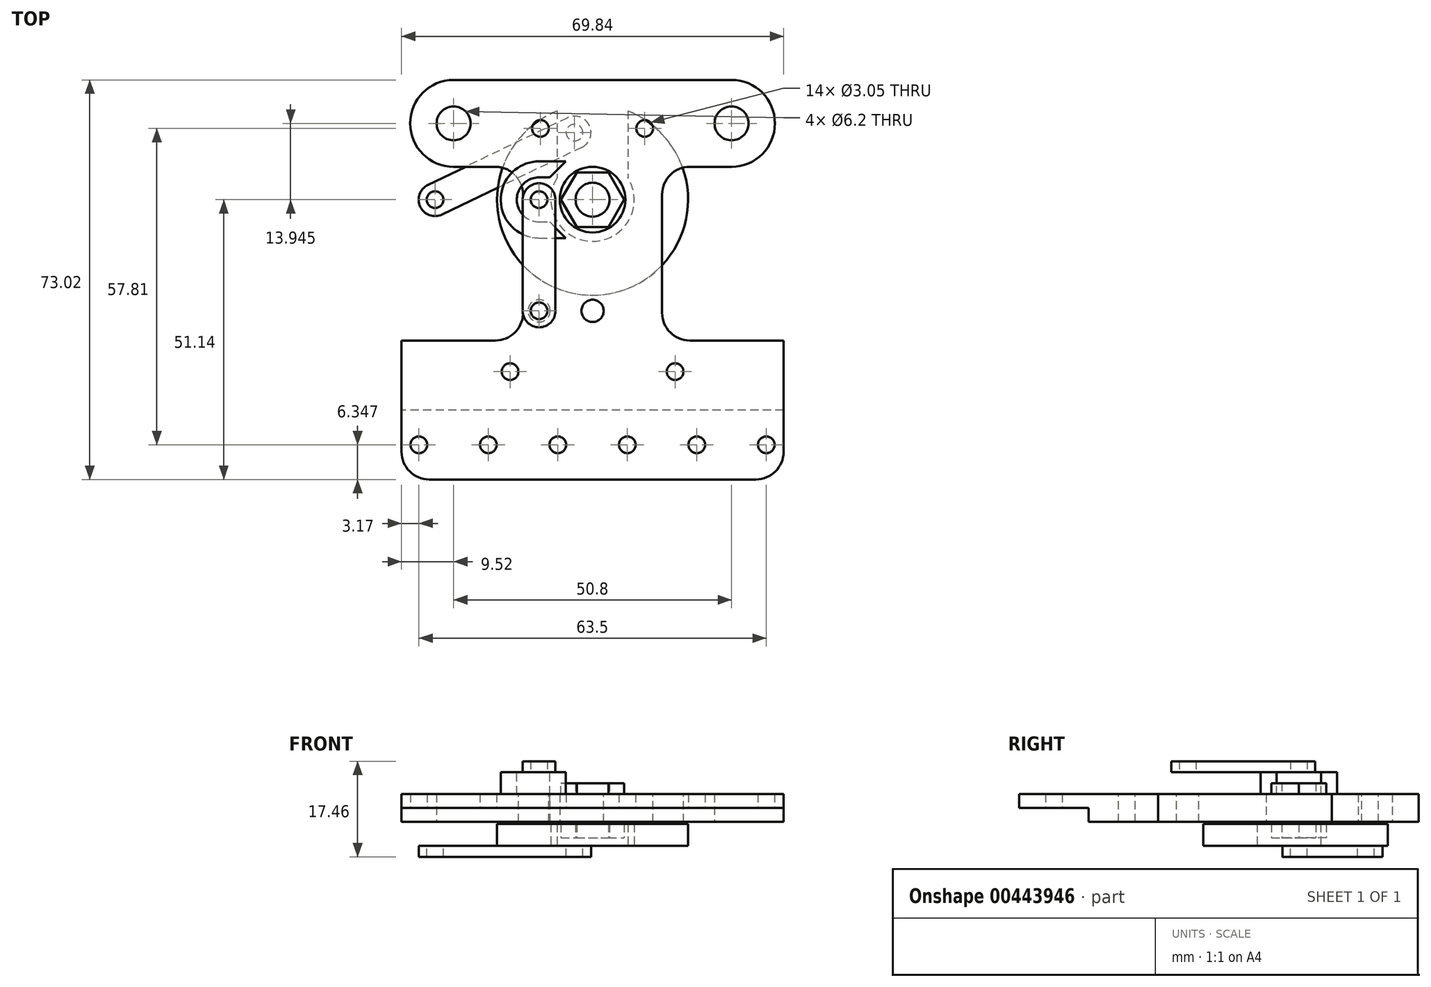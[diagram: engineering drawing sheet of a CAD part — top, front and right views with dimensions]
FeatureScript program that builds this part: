
annotation { "Feature Type Name" : "Feature", "Feature Type Description" : "" }
export const myFeature = defineFeature(function(context is Context, id is Id, definition is map)
    precondition{}
    {
        {
            var Q0;
            Q0=qCreatedBy(makeId("Top.planeOp"),FACE);
            var sketch = newSketch(context, id + "F0", { "sketchPlane" : qUnion([Q0])});
            skLineSegment(sketch, "E0.bottom", {"start": v(-34.92, 36.51) * mm, "end": v(34.93, 36.51) * mm});
            skLineSegment(sketch, "E0.top", {"start": v(-34.93, -36.51) * mm, "end": v(34.92, -36.51) * mm});
            skLineSegment(sketch, "E0.left", {"start": v(-34.92, 36.51) * mm, "end": v(-34.93, -36.51) * mm});
            skLineSegment(sketch, "E0.right", {"start": v(34.93, 36.51) * mm, "end": v(34.92, -36.51) * mm});
            skPoint(sketch, "E0.middle", {"position": v(0, 0) * mm});
            skSolve(sketch);
        }
        {
            var Q0;
            Q0=qSketchRegion(id+"F0",true);
            extrude(context, id + "F1", {"entities" : qUnion([Q0]), "depth" : 5.08 * mm});
        }
        {
            var Q0;
            Q0=makeQuery(id+"F1.opExtrude","SWEPT_FACE",FACE,{"disambiguationData":[OSD([sQuery(id+"F0.wireOp",EDGE,"E0.left")])]});
            var sketch = newSketch(context, id + "F2", { "sketchPlane" : qUnion([Q0])});
            skLineSegment(sketch, "E1.bottom", {"start": v(36.51, 2.54) * mm, "end": v(23.81, 2.54) * mm});
            skLineSegment(sketch, "E1.top", {"start": v(36.51, 0) * mm, "end": v(23.81, 0) * mm});
            skLineSegment(sketch, "E1.left", {"start": v(36.51, 2.54) * mm, "end": v(36.51, 0) * mm});
            skLineSegment(sketch, "E1.right", {"start": v(23.81, 2.54) * mm, "end": v(23.81, 0) * mm});
            skSolve(sketch);
        }
        {
            var Q0;
            Q0=qSketchRegion(id+"F2",true);
            extrude(context, id + "F3", {"entities" : qUnion([Q0]), "operationType" : NewBodyOperationType.REMOVE, "endBound" : BoundingType.THROUGH_ALL, "oppositeDirection" : true, "depth" : 25.4 * mm});
        }
        {
            var Q0;
            Q0=makeQuery(id+"F1.opExtrude","CAP_FACE",FACE,{"disambiguationData":[OSD([sQuery(id+"F0.wireOp",EDGE,"E0.bottom"),sQuery(id+"F0.wireOp",EDGE,"E0.top"),sQuery(id+"F0.wireOp",EDGE,"E0.left"),sQuery(id+"F0.wireOp",EDGE,"E0.right")])],"isStart":true});
            var sketch = newSketch(context, id + "F4", { "sketchPlane" : qUnion([Q0])});
            skLineSegment(sketch, "E2", {"start": v(-25.4, -28.58) * mm, "end": v(0, -28.58) * mm, "construction": true});
            skLineSegment(sketch, "E3", {"start": v(0, -28.58) * mm, "end": v(25.4, -28.58) * mm, "construction": true});
            skLineSegment(sketch, "E4", {"start": v(0, -28.58) * mm, "end": v(0, -14.63) * mm, "construction": true});
            skCircle(sketch, "E5", {"center": v(-25.4, -28.58) * mm, "radius": 3.1 * mm});
            skCircle(sketch, "E6", {"center": v(0, -14.63) * mm, "radius": 6 * mm});
            skCircle(sketch, "E7", {"center": v(25.4, -28.58) * mm, "radius": 3.1 * mm});
            skArc(sketch, "E8", {"start": v(-25.4, -36.51) * mm, "mid": v(-33.34, -28.58) * mm, "end": v(-25.4, -20.64) * mm});
            skArc(sketch, "E9", {"start": v(25.4, -36.51) * mm, "mid": v(33.34, -28.58) * mm, "end": v(25.4, -20.64) * mm});
            skLineSegment(sketch, "E10", {"start": v(-25.4, -20.64) * mm, "end": v(-12.7, -20.64) * mm});
            skLineSegment(sketch, "E11", {"start": v(-12.7, -20.64) * mm, "end": v(-12.7, 11.11) * mm});
            skLineSegment(sketch, "E12", {"start": v(-12.7, 11.11) * mm, "end": v(-34.93, 11.11) * mm});
            skLineSegment(sketch, "E13", {"start": v(12.7, 11.11) * mm, "end": v(34.92, 11.11) * mm});
            skLineSegment(sketch, "E14", {"start": v(34.92, 11.11) * mm, "end": v(34.93, -36.51) * mm});
            skLineSegment(sketch, "E15", {"start": v(34.93, -36.51) * mm, "end": v(25.4, -36.51) * mm});
            skLineSegment(sketch, "E16", {"start": v(-25.4, -36.51) * mm, "end": v(-34.92, -36.51) * mm});
            skLineSegment(sketch, "E17", {"start": v(-34.92, -36.51) * mm, "end": v(-34.93, 11.11) * mm});
            skLineSegment(sketch, "E18", {"start": v(25.4, -20.64) * mm, "end": v(12.7, -20.64) * mm});
            skLineSegment(sketch, "E19", {"start": v(12.7, -20.64) * mm, "end": v(12.7, 11.11) * mm});
            skLineSegment(sketch, "E20", {"start": v(-25.4, -28.58) * mm, "end": v(-25.4, -14.63) * mm, "construction": true});
            skLineSegment(sketch, "E21", {"start": v(0, -14.63) * mm, "end": v(-12.7, -14.63) * mm, "construction": true});
            skLineSegment(sketch, "E22", {"start": v(0, -14.63) * mm, "end": v(12.7, -14.63) * mm, "construction": true});
            skSolve(sketch);
        }
        {
            var Q0;
            Q0=qSketchRegion(id+"F4",true);
            extrude(context, id + "F5", {"entities" : qUnion([Q0]), "operationType" : NewBodyOperationType.REMOVE, "endBound" : BoundingType.UP_TO_NEXT, "oppositeDirection" : true, "depth" : 25.4 * mm});
        }
        {
            var Q0;
            Q0=makeQuery(id+"F5.boolean.opBoolean","COPY",EDGE,{"derivedFrom":makeQuery(id+"F5.opExtrude","SWEPT_EDGE",EDGE,{"disambiguationData":[OSD([sQuery(id+"F4.wireOp",EDGE,"E10"),sQuery(id+"F4.wireOp",EDGE,"E11")])]})});
            var Q1;
            Q1=makeQuery(id+"F5.boolean.opBoolean","COPY",EDGE,{"derivedFrom":makeQuery(id+"F5.opExtrude","SWEPT_EDGE",EDGE,{"disambiguationData":[OSD([sQuery(id+"F4.wireOp",EDGE,"E18"),sQuery(id+"F4.wireOp",EDGE,"E19")])]})});
            var Q2;
            Q2=makeQuery(id+"F5.boolean.opBoolean","COPY",EDGE,{"derivedFrom":makeQuery(id+"F5.opExtrude","SWEPT_EDGE",EDGE,{"disambiguationData":[OSD([sQuery(id+"F4.wireOp",EDGE,"E13"),sQuery(id+"F4.wireOp",EDGE,"E19")])]})});
            var Q3;
            Q3=makeQuery(id+"F5.boolean.opBoolean","COPY",EDGE,{"derivedFrom":makeQuery(id+"F5.opExtrude","SWEPT_EDGE",EDGE,{"disambiguationData":[OSD([sQuery(id+"F4.wireOp",EDGE,"E11"),sQuery(id+"F4.wireOp",EDGE,"E12")])]})});
            var Q4;
            Q4=makeQuery(id+"F5.boolean.opBoolean","COPY",EDGE,{"derivedFrom":makeQuery(id+"F5.opExtrude","SWEPT_EDGE",EDGE,{"disambiguationData":[OSD([sQuery(id+"F0.wireOp",EDGE,"E0.right"),sQuery(id+"F4.wireOp",EDGE,"E13"),sQuery(id+"F4.wireOp",EDGE,"E14")])]})});
            var Q5;
            Q5=makeQuery(id+"F5.boolean.opBoolean","COPY",EDGE,{"derivedFrom":makeQuery(id+"F5.opExtrude","SWEPT_EDGE",EDGE,{"disambiguationData":[OSD([sQuery(id+"F0.wireOp",EDGE,"E0.left"),sQuery(id+"F4.wireOp",EDGE,"E12"),sQuery(id+"F4.wireOp",EDGE,"E17")])]})});
            var Q6;
            Q6=makeQuery(id+"F1.opExtrude","SWEPT_EDGE",EDGE,{"disambiguationData":[OSD([sQuery(id+"F0.wireOp",EDGE,"E0.top"),sQuery(id+"F0.wireOp",EDGE,"E0.left")])]});
            var Q7;
            Q7=makeQuery(id+"F1.opExtrude","SWEPT_EDGE",EDGE,{"disambiguationData":[OSD([sQuery(id+"F0.wireOp",EDGE,"E0.top"),sQuery(id+"F0.wireOp",EDGE,"E0.right")])]});
            fillet(context, id + "F6", {"entities" : qUnion([Q0, Q1, Q2, Q3, Q4, Q5, Q6, Q7]), "radius" : 5.08 * mm, "tangentPropagation" : true, "allowEdgeOverflow" : false});
        }
        {
            var Q0;
            Q0=makeQuery(id+"F1.opExtrude","CAP_FACE",FACE,{"disambiguationData":[OSD([sQuery(id+"F0.wireOp",EDGE,"E0.bottom"),sQuery(id+"F0.wireOp",EDGE,"E0.top"),sQuery(id+"F0.wireOp",EDGE,"E0.left"),sQuery(id+"F0.wireOp",EDGE,"E0.right")])],"isStart":true});
            cPlane(context, id + "F7", {"entities" : qUnion([Q0]), "cplaneType" : CPlaneType.OFFSET, "offset" : 0.38 * mm, "width" : 152.4 * mm, "height" : 152.4 * mm});
        }
        {
            var Q0;
            Q0=qCreatedBy(id+"F7.planeOp",FACE);
            var sketch = newSketch(context, id + "F8", { "sketchPlane" : qUnion([Q0])});
            skCircle(sketch, "E23", {"center": v(0, -14.63) * mm, "radius": 17.46 * mm});
            skSolve(sketch);
        }
        {
            var Q0;
            Q0=makeQuery(id+"F8.imprint","IMPRINT",FACE,{"disambiguationData":[TD([[makeQuery(id+"F8.imprint","IMPRINT",EDGE,{"derivedFrom":sQuery(id+"F8.wireOp",EDGE,"7JbUnUjg-stlZ-eKcx-IOZO-H9E1dYresgRF.bottom")}),-1.0]])]});
            var Q1;
            Q1=makeQuery(id+"F8.imprint","IMPRINT",FACE,{"disambiguationData":[TD([[makeQuery(id+"F8.imprint","IMPRINT",EDGE,{"derivedFrom":sQuery(id+"F8.wireOp",EDGE,"E23")}),1.0]])]});
            var Q2;
            Q2=sQuery(id+"F8.wireOp",EDGE,"7JbUnUjg-stlZ-eKcx-IOZO-H9E1dYresgRF.bottom");
            var Q3;
            Q3=sQuery(id+"F8.wireOp",EDGE,"7JbUnUjg-stlZ-eKcx-IOZO-H9E1dYresgRF.top");
            extrude(context, id + "F9", {"entities" : qUnion([Q0, Q1]), "surfaceEntities" : qUnion([Q2, Q3]), "depth" : 4 * mm});
        }
        {
            var Q0;
            Q0=makeQuery(id+"F9.opExtrude","CAP_FACE",FACE,{"disambiguationData":[OSD([sQuery(id+"F8.wireOp",EDGE,"E23")])],"isStart":false});
            var sketch = newSketch(context, id + "F10", { "sketchPlane" : qUnion([Q0])});
            skCircle(sketch, "E24", {"center": v(0, -14.63) * mm, "radius": 3.1 * mm});
            skSolve(sketch);
        }
        {
            var Q0;
            Q0=makeQuery(id+"F10.imprint","IMPRINT",FACE,{"disambiguationData":[TD([[makeQuery(id+"F10.imprint","IMPRINT",EDGE,{"derivedFrom":sQuery(id+"F10.wireOp",EDGE,"E24")}),1.0]])]});
            extrude(context, id + "F11", {"entities" : qUnion([Q0]), "operationType" : NewBodyOperationType.REMOVE, "oppositeDirection" : true, "depth" : 25.4 * mm});
        }
        {
            var Q0;
            Q0=makeQuery(id+"F9.opExtrude","CAP_FACE",FACE,{"disambiguationData":[OSD([sQuery(id+"F8.wireOp",EDGE,"E23")])],"isStart":false});
            var sketch = newSketch(context, id + "F12", { "sketchPlane" : qUnion([Q0])});
            skCircle(sketch, "E25.cCircle", {"center": v(0, -14.63) * mm, "radius": 5 * mm, "construction": true});
            skLineSegment(sketch, "E25.0", {"start": v(2.89, -9.63) * mm, "end": v(5.77, -14.63) * mm});
            skLineSegment(sketch, "E25.1", {"start": v(5.77, -14.63) * mm, "end": v(2.89, -19.63) * mm});
            skLineSegment(sketch, "E25.2", {"start": v(2.89, -19.63) * mm, "end": v(-2.89, -19.63) * mm});
            skLineSegment(sketch, "E25.3", {"start": v(-2.89, -19.63) * mm, "end": v(-5.77, -14.63) * mm});
            skLineSegment(sketch, "E25.4", {"start": v(-5.77, -14.63) * mm, "end": v(-2.89, -9.63) * mm});
            skLineSegment(sketch, "E25.5", {"start": v(-2.89, -9.63) * mm, "end": v(2.89, -9.63) * mm});
            skPoint(sketch, "E25.0.midPoint", {"position": v(4.33, -12.13) * mm});
            skSolve(sketch);
        }
        {
            var Q0;
            Q0=makeQuery(id+"F3.boolean.opBoolean","COPY",FACE,{"derivedFrom":makeQuery(id+"F3.opExtrude","SWEPT_FACE",FACE,{"disambiguationData":[OSD([sQuery(id+"F2.wireOp",EDGE,"E1.bottom")])]})});
            var sketch = newSketch(context, id + "F13", { "sketchPlane" : qUnion([Q0])});
            skLineSegment(sketch, "E26", {"start": v(-31.75, 30.16) * mm, "end": v(-19.05, 30.16) * mm, "construction": true});
            skLineSegment(sketch, "E27", {"start": v(-19.05, 30.16) * mm, "end": v(-6.35, 30.16) * mm, "construction": true});
            skLineSegment(sketch, "E28", {"start": v(-6.35, 30.16) * mm, "end": v(6.35, 30.16) * mm, "construction": true});
            skLineSegment(sketch, "E29", {"start": v(6.35, 30.16) * mm, "end": v(19.05, 30.16) * mm, "construction": true});
            skLineSegment(sketch, "E30", {"start": v(19.05, 30.16) * mm, "end": v(31.75, 30.16) * mm, "construction": true});
            skLineSegment(sketch, "E31", {"start": v(31.75, 30.16) * mm, "end": v(34.92, 30.16) * mm, "construction": true});
            skLineSegment(sketch, "E32", {"start": v(-31.75, 30.16) * mm, "end": v(-34.93, 30.16) * mm, "construction": true});
            skCircle(sketch, "E33", {"center": v(-31.75, 30.16) * mm, "radius": 1.52 * mm});
            skCircle(sketch, "E34", {"center": v(-19.05, 30.16) * mm, "radius": 1.52 * mm});
            skCircle(sketch, "E35", {"center": v(-6.35, 30.16) * mm, "radius": 1.52 * mm});
            skCircle(sketch, "E36", {"center": v(6.35, 30.16) * mm, "radius": 1.52 * mm});
            skCircle(sketch, "E37", {"center": v(19.05, 30.16) * mm, "radius": 1.52 * mm});
            skCircle(sketch, "E38", {"center": v(31.75, 30.16) * mm, "radius": 1.52 * mm});
            skLineSegment(sketch, "E39", {"start": v(-29.85, 36.51) * mm, "end": v(-29.85, 23.81) * mm, "construction": true});
            skPoint(sketch, "E40", {"position": v(-29.85, 30.16) * mm});
            skSolve(sketch);
        }
        {
            var Q0;
            Q0=makeQuery(id+"F12.imprint","IMPRINT",FACE,{"disambiguationData":[TD([[makeQuery(id+"F12.imprint","IMPRINT",EDGE,{"derivedFrom":sQuery(id+"F12.wireOp",EDGE,"E25.0")}),-1.0]])]});
            extrude(context, id + "F14", {"entities" : qUnion([Q0]), "operationType" : NewBodyOperationType.REMOVE, "oppositeDirection" : true, "depth" : 1.5 * mm});
        }
        {
            var Q0;
            Q0=makeQuery(id+"F9.opExtrude","CAP_FACE",FACE,{"disambiguationData":[OSD([sQuery(id+"F8.wireOp",EDGE,"E23")])],"isStart":false});
            var sketch = newSketch(context, id + "F15", { "sketchPlane" : qUnion([Q0])});
            skLineSegment(sketch, "E41", {"start": v(0, -14.63) * mm, "end": v(-3.29, -26.9) * mm, "construction": true});
            skLineSegment(sketch, "E42", {"start": v(-25.4, -28.58) * mm, "end": v(-25.4, -14.63) * mm, "construction": true});
            skLineSegment(sketch, "E43", {"start": v(-25.4, -14.63) * mm, "end": v(-28.78, -14.63) * mm, "construction": true});
            skLineSegment(sketch, "E44", {"start": v(-28.78, -14.63) * mm, "end": v(-3.29, -26.9) * mm, "construction": true});
            skLineSegment(sketch, "E45", {"start": v(0, -14.63) * mm, "end": v(3.29, -26.9) * mm, "construction": true});
            skCircle(sketch, "E46", {"center": v(-3.29, -26.9) * mm, "radius": 1.52 * mm});
            skCircle(sketch, "E47", {"center": v(3.29, -26.9) * mm, "radius": 1.52 * mm});
            skSolve(sketch);
        }
        {
            var Q0;
            Q0=makeQuery(id+"F15.imprint","IMPRINT",FACE,{"disambiguationData":[TD([[makeQuery(id+"F15.imprint","IMPRINT",EDGE,{"derivedFrom":sQuery(id+"F15.wireOp",EDGE,"E46")}),1.0]])]});
            var Q1;
            Q1=makeQuery(id+"F15.imprint","IMPRINT",FACE,{"disambiguationData":[TD([[makeQuery(id+"F15.imprint","IMPRINT",EDGE,{"derivedFrom":sQuery(id+"F15.wireOp",EDGE,"E47")}),1.0]])]});
            var Q2;
            Q2=sQuery(id+"F15.wireOp",EDGE,"E44");
            var Q3;
            Q3=sQuery(id+"F15.wireOp",EDGE,"E41");
            var Q4;
            Q4=sQuery(id+"F15.wireOp",EDGE,"E45");
            var Q5;
            Q5=sQuery(id+"F15.wireOp",EDGE,"E43");
            var Q6;
            Q6=sQuery(id+"F15.wireOp",EDGE,"E42");
            extrude(context, id + "F16", {"entities" : qUnion([Q0, Q1]), "operationType" : NewBodyOperationType.REMOVE, "surfaceEntities" : qUnion([Q2, Q3, Q4, Q5, Q6]), "endBound" : BoundingType.UP_TO_NEXT, "oppositeDirection" : true, "depth" : 25.4 * mm});
        }
        {
            var Q0;
            Q0=makeQuery(id+"F9.opExtrude","CAP_FACE",FACE,{"disambiguationData":[OSD([sQuery(id+"F8.wireOp",EDGE,"E23")])],"isStart":false});
            var sketch = newSketch(context, id + "F17", { "sketchPlane" : qUnion([Q0])});
            skArc(sketch, "E48", {"start": v(-6.48, -18.64) * mm, "mid": v(0, -7.01) * mm, "end": v(6.48, -18.64) * mm});
            skLineSegment(sketch, "E49", {"start": v(-6.48, -18.64) * mm, "end": v(-6.48, -30.85) * mm});
            skLineSegment(sketch, "E50", {"start": v(6.48, -18.64) * mm, "end": v(6.48, -30.85) * mm});
            skSolve(sketch);
        }
        {
            var Q0;
            Q0=qSketchRegion(id+"F17",true);
            var Q1;
            Q1=makeQuery(id+"F17.imprint","IMPRINT",FACE,{"disambiguationData":[TD([[makeQuery(id+"F17.imprint","IMPRINT",EDGE,{"derivedFrom":sQuery(id+"F17.wireOp",EDGE,"E48")}),1.0]])]});
            extrude(context, id + "F18", {"entities" : qUnion([Q0, Q1]), "operationType" : NewBodyOperationType.REMOVE, "endBound" : BoundingType.UP_TO_NEXT, "oppositeDirection" : true, "depth" : 25.4 * mm});
        }
        {
            var Q0;
            Q0=makeQuery(id+"F9.opExtrude","CAP_FACE",FACE,{"disambiguationData":[OSD([sQuery(id+"F8.wireOp",EDGE,"E23")])],"isStart":false});
            var sketch = newSketch(context, id + "F19", { "sketchPlane" : qUnion([Q0])});
            skLineSegment(sketch, "E51", {"start": v(-3.29, -26.9) * mm, "end": v(-28.78, -14.63) * mm, "construction": true});
            skLineSegment(sketch, "E52", {"start": v(-28.78, -14.63) * mm, "end": v(-25.4, -14.63) * mm, "construction": true});
            skLineSegment(sketch, "E53", {"start": v(-25.4, -14.63) * mm, "end": v(-25.4, -28.58) * mm, "construction": true});
            skArc(sketch, "E54", {"start": v(-30.08, -17.33) * mm, "mid": v(-31.48, -13.33) * mm, "end": v(-27.48, -11.93) * mm});
            skArc(sketch, "E55", {"start": v(-1.99, -24.2) * mm, "mid": v(-0.58, -28.2) * mm, "end": v(-4.59, -29.6) * mm});
            skLineSegment(sketch, "E56", {"start": v(-1.99, -24.2) * mm, "end": v(-27.48, -11.93) * mm});
            skLineSegment(sketch, "E57", {"start": v(-4.59, -29.6) * mm, "end": v(-30.08, -17.33) * mm});
            skCircle(sketch, "E58", {"center": v(-3.29, -26.9) * mm, "radius": 1.52 * mm});
            skCircle(sketch, "E59", {"center": v(-28.78, -14.63) * mm, "radius": 1.52 * mm});
            skSolve(sketch);
        }
        {
            var Q0;
            Q0=qSketchRegion(id+"F19",true);
            extrude(context, id + "F20", {"entities" : qUnion([Q0]), "depth" : 2 * mm});
        }
        {
            var Q0;
            Q0=makeQuery(id+"F13.imprint","IMPRINT",FACE,{"disambiguationData":[TD([[makeQuery(id+"F13.imprint","IMPRINT",EDGE,{"derivedFrom":sQuery(id+"F13.wireOp",EDGE,"E33")}),1.0]])]});
            var Q1;
            Q1=makeQuery(id+"F13.imprint","IMPRINT",FACE,{"disambiguationData":[TD([[makeQuery(id+"F13.imprint","IMPRINT",EDGE,{"derivedFrom":sQuery(id+"F13.wireOp",EDGE,"E34")}),1.0]])]});
            var Q2;
            Q2=makeQuery(id+"F13.imprint","IMPRINT",FACE,{"disambiguationData":[TD([[makeQuery(id+"F13.imprint","IMPRINT",EDGE,{"derivedFrom":sQuery(id+"F13.wireOp",EDGE,"E35")}),1.0]])]});
            var Q3;
            Q3=makeQuery(id+"F13.imprint","IMPRINT",FACE,{"disambiguationData":[TD([[makeQuery(id+"F13.imprint","IMPRINT",EDGE,{"derivedFrom":sQuery(id+"F13.wireOp",EDGE,"E36")}),1.0]])]});
            var Q4;
            Q4=makeQuery(id+"F13.imprint","IMPRINT",FACE,{"disambiguationData":[TD([[makeQuery(id+"F13.imprint","IMPRINT",EDGE,{"derivedFrom":sQuery(id+"F13.wireOp",EDGE,"E37")}),1.0]])]});
            var Q5;
            Q5=makeQuery(id+"F13.imprint","IMPRINT",FACE,{"disambiguationData":[TD([[makeQuery(id+"F13.imprint","IMPRINT",EDGE,{"derivedFrom":sQuery(id+"F13.wireOp",EDGE,"E38")}),1.0]])]});
            extrude(context, id + "F21", {"entities" : qUnion([Q0, Q1, Q2, Q3, Q4, Q5]), "operationType" : NewBodyOperationType.REMOVE, "endBound" : BoundingType.UP_TO_NEXT, "oppositeDirection" : true, "depth" : 25.4 * mm});
        }
        {
            var Q0;
            Q0=makeQuery(id+"F1.opExtrude","CAP_FACE",FACE,{"disambiguationData":[OSD([sQuery(id+"F0.wireOp",EDGE,"E0.bottom"),sQuery(id+"F0.wireOp",EDGE,"E0.top"),sQuery(id+"F0.wireOp",EDGE,"E0.left"),sQuery(id+"F0.wireOp",EDGE,"E0.right")])],"isStart":false});
            var sketch = newSketch(context, id + "F22", { "sketchPlane" : qUnion([Q0])});
            skCircle(sketch, "E60", {"center": v(0, 14.63) * mm, "radius": 3.1 * mm});
            skCircle(sketch, "E61", {"center": v(-9.78, 14.63) * mm, "radius": 1.52 * mm});
            skLineSegment(sketch, "E62", {"start": v(-9.78, 14.63) * mm, "end": v(0, 14.63) * mm, "construction": true});
            skLineSegment(sketch, "E63.bottom", {"start": v(-9.78, 21.63) * mm, "end": v(0, 21.63) * mm});
            skLineSegment(sketch, "E63.top", {"start": v(-9.78, 7.63) * mm, "end": v(0, 7.63) * mm});
            skLineSegment(sketch, "E63.left", {"start": v(-9.78, 21.63) * mm, "end": v(-9.78, 7.63) * mm, "construction": true});
            skLineSegment(sketch, "E63.right", {"start": v(0, 21.63) * mm, "end": v(0, 7.63) * mm, "construction": true});
            skPoint(sketch, "E63.middle", {"position": v(-4.89, 14.63) * mm});
            skArc(sketch, "E64", {"start": v(-9.78, 7.63) * mm, "mid": v(-16.78, 14.63) * mm, "end": v(-9.78, 21.63) * mm});
            skArc(sketch, "E65", {"start": v(0, 21.63) * mm, "mid": v(7, 14.63) * mm, "end": v(0, 7.63) * mm});
            skSolve(sketch);
        }
        {
            var Q0;
            Q0=qSketchRegion(id+"F22",true);
            extrude(context, id + "F23", {"entities" : qUnion([Q0]), "depth" : 4 * mm});
        }
        {
            var Q0;
            Q0=makeQuery(id+"F23.opExtrude","CAP_FACE",FACE,{"disambiguationData":[OSD([sQuery(id+"F22.wireOp",EDGE,"E60"),sQuery(id+"F22.wireOp",EDGE,"E61"),sQuery(id+"F22.wireOp",EDGE,"E63.bottom"),sQuery(id+"F22.wireOp",EDGE,"E63.top"),sQuery(id+"F22.wireOp",EDGE,"E64"),sQuery(id+"F22.wireOp",EDGE,"E65")])],"isStart":false});
            var sketch = newSketch(context, id + "F24", { "sketchPlane" : qUnion([Q0])});
            skCircle(sketch, "E66.cCircle", {"center": v(0, 14.63) * mm, "radius": 5 * mm, "construction": true});
            skLineSegment(sketch, "E66.0", {"start": v(-2.89, 19.63) * mm, "end": v(2.89, 19.63) * mm});
            skLineSegment(sketch, "E66.1", {"start": v(2.89, 19.63) * mm, "end": v(5.77, 14.63) * mm});
            skLineSegment(sketch, "E66.2", {"start": v(5.77, 14.63) * mm, "end": v(2.89, 9.63) * mm});
            skLineSegment(sketch, "E66.3", {"start": v(2.89, 9.63) * mm, "end": v(-2.89, 9.63) * mm});
            skLineSegment(sketch, "E66.4", {"start": v(-2.89, 9.63) * mm, "end": v(-5.77, 14.63) * mm});
            skLineSegment(sketch, "E66.5", {"start": v(-5.77, 14.63) * mm, "end": v(-2.89, 19.63) * mm});
            skPoint(sketch, "E66.0.midPoint", {"position": v(0, 19.63) * mm});
            skSolve(sketch);
        }
        {
            var Q0;
            Q0=qSketchRegion(id+"F24",true);
            extrude(context, id + "F25", {"entities" : qUnion([Q0]), "operationType" : NewBodyOperationType.REMOVE, "oppositeDirection" : true, "depth" : 2 * mm});
        }
        {
            var Q0;
            Q0=makeQuery(id+"F23.opExtrude","CAP_FACE",FACE,{"disambiguationData":[OSD([sQuery(id+"F22.wireOp",EDGE,"E60"),sQuery(id+"F22.wireOp",EDGE,"E61"),sQuery(id+"F22.wireOp",EDGE,"E63.bottom"),sQuery(id+"F22.wireOp",EDGE,"E63.top"),sQuery(id+"F22.wireOp",EDGE,"E64"),sQuery(id+"F22.wireOp",EDGE,"E65")])],"isStart":false});
            var sketch = newSketch(context, id + "F26", { "sketchPlane" : qUnion([Q0])});
            skArc(sketch, "E67", {"start": v(-9.78, 10.57) * mm, "mid": v(-13.84, 14.63) * mm, "end": v(-9.78, 18.7) * mm});
            skLineSegment(sketch, "E68", {"start": v(-9.78, 18.7) * mm, "end": v(-7.83, 18.7) * mm});
            skLineSegment(sketch, "E69", {"start": v(-7.83, 18.7) * mm, "end": v(-4.89, 21.63) * mm});
            skLineSegment(sketch, "E70", {"start": v(-9.78, 10.57) * mm, "end": v(-7.83, 10.57) * mm});
            skLineSegment(sketch, "E71", {"start": v(-7.83, 10.57) * mm, "end": v(-4.89, 7.63) * mm});
            skSolve(sketch);
        }
        {
            var Q0;
            Q0=qSketchRegion(id+"F26",true);
            var Q1;
            Q1=makeQuery(id+"F26.imprint","IMPRINT",FACE,{"disambiguationData":[TD([[makeQuery(id+"F26.imprint","IMPRINT",EDGE,{"derivedFrom":sQuery(id+"F26.wireOp",EDGE,"E67")}),1.0]])]});
            extrude(context, id + "F27", {"entities" : qUnion([Q0, Q1]), "operationType" : NewBodyOperationType.REMOVE, "endBound" : BoundingType.UP_TO_NEXT, "oppositeDirection" : true, "depth" : 25.4 * mm});
        }
        {
            var Q0;
            Q0=makeQuery(id+"F1.opExtrude","CAP_FACE",FACE,{"disambiguationData":[OSD([sQuery(id+"F0.wireOp",EDGE,"E0.bottom"),sQuery(id+"F0.wireOp",EDGE,"E0.top"),sQuery(id+"F0.wireOp",EDGE,"E0.left"),sQuery(id+"F0.wireOp",EDGE,"E0.right")])],"isStart":false});
            var sketch = newSketch(context, id + "F28", { "sketchPlane" : qUnion([Q0])});
            skCircle(sketch, "E72", {"center": v(0, -5.69) * mm, "radius": 2.03 * mm});
            skLineSegment(sketch, "E73", {"start": v(0, 14.63) * mm, "end": v(0, -5.69) * mm, "construction": true});
            skCircle(sketch, "E74", {"center": v(-9.78, -5.69) * mm, "radius": 2.03 * mm});
            skLineSegment(sketch, "E75", {"start": v(-9.78, -5.69) * mm, "end": v(-9.78, 14.63) * mm, "construction": true});
            skSolve(sketch);
        }
        {
            var Q0;
            Q0=qSketchRegion(id+"F28",true);
            extrude(context, id + "F29", {"entities" : qUnion([Q0]), "operationType" : NewBodyOperationType.REMOVE, "endBound" : BoundingType.UP_TO_NEXT, "oppositeDirection" : true, "depth" : 25.4 * mm});
        }
        {
            var Q0;
            Q0=makeQuery(id+"F1.opExtrude","CAP_FACE",FACE,{"disambiguationData":[OSD([sQuery(id+"F0.wireOp",EDGE,"E0.bottom"),sQuery(id+"F0.wireOp",EDGE,"E0.top"),sQuery(id+"F0.wireOp",EDGE,"E0.left"),sQuery(id+"F0.wireOp",EDGE,"E0.right")])],"isStart":false});
            var sketch = newSketch(context, id + "F30", { "sketchPlane" : qUnion([Q0])});
            skLineSegment(sketch, "E76.bottom", {"start": v(15.08, 27.65) * mm, "end": v(-15.08, 27.65) * mm, "construction": true});
            skLineSegment(sketch, "E76.top", {"start": v(15.08, -16.8) * mm, "end": v(-15.08, -16.8) * mm, "construction": true});
            skLineSegment(sketch, "E76.left", {"start": v(15.08, 27.65) * mm, "end": v(15.08, -16.8) * mm, "construction": true});
            skLineSegment(sketch, "E76.right", {"start": v(-15.08, 27.65) * mm, "end": v(-15.08, -16.8) * mm, "construction": true});
            skPoint(sketch, "E76.middle", {"position": v(0, 5.42) * mm});
            skLineSegment(sketch, "E77", {"start": v(0, -5.69) * mm, "end": v(0, 5.42) * mm, "construction": true});
            skCircle(sketch, "E78", {"center": v(15.08, -16.8) * mm, "radius": 1.52 * mm});
            skCircle(sketch, "E79", {"center": v(-15.08, -16.8) * mm, "radius": 1.52 * mm});
            skLineSegment(sketch, "E80", {"start": v(-15.08, -16.8) * mm, "end": v(-9.53, 27.65) * mm, "construction": true});
            skLineSegment(sketch, "E81", {"start": v(-9.53, 27.65) * mm, "end": v(0, -16.8) * mm, "construction": true});
            skLineSegment(sketch, "E82", {"start": v(0, -16.8) * mm, "end": v(9.52, 27.65) * mm, "construction": true});
            skLineSegment(sketch, "E83", {"start": v(9.52, 27.65) * mm, "end": v(15.08, -16.8) * mm, "construction": true});
            skCircle(sketch, "E84", {"center": v(-9.53, 27.65) * mm, "radius": 1.52 * mm});
            skCircle(sketch, "E85", {"center": v(9.52, 27.65) * mm, "radius": 1.52 * mm});
            skSolve(sketch);
        }
        {
            var Q0;
            Q0=qSketchRegion(id+"F30",true);
            extrude(context, id + "F31", {"entities" : qUnion([Q0]), "operationType" : NewBodyOperationType.REMOVE, "endBound" : BoundingType.UP_TO_NEXT, "oppositeDirection" : true, "depth" : 25.4 * mm});
        }
        {
            var Q0;
            Q0=makeQuery(id+"F23.opExtrude","CAP_FACE",FACE,{"disambiguationData":[OSD([sQuery(id+"F22.wireOp",EDGE,"E60"),sQuery(id+"F22.wireOp",EDGE,"E61"),sQuery(id+"F22.wireOp",EDGE,"E63.bottom"),sQuery(id+"F22.wireOp",EDGE,"E63.top"),sQuery(id+"F22.wireOp",EDGE,"E64"),sQuery(id+"F22.wireOp",EDGE,"E65")])],"isStart":true});
            var sketch = newSketch(context, id + "F32", { "sketchPlane" : qUnion([Q0])});
            skCircle(sketch, "E86", {"center": v(-9.78, -14.63) * mm, "radius": 2.8 * mm});
            skSolve(sketch);
        }
        {
            var Q0;
            Q0=qSketchRegion(id+"F32",true);
            extrude(context, id + "F33", {"entities" : qUnion([Q0]), "operationType" : NewBodyOperationType.REMOVE, "oppositeDirection" : true, "depth" : 2.54 * mm});
        }
        {
            var Q0;
            Q0=makeQuery(id+"F9.opExtrude","CAP_FACE",FACE,{"disambiguationData":[OSD([sQuery(id+"F8.wireOp",EDGE,"E23")])],"isStart":true});
            var sketch = newSketch(context, id + "F34", { "sketchPlane" : qUnion([Q0])});
            skCircle(sketch, "E87", {"center": v(-3.29, 26.9) * mm, "radius": 2.8 * mm});
            skCircle(sketch, "E88", {"center": v(3.29, 26.9) * mm, "radius": 2.8 * mm});
            skSolve(sketch);
        }
        {
            var Q0;
            Q0=qSketchRegion(id+"F34",true);
            extrude(context, id + "F35", {"entities" : qUnion([Q0]), "operationType" : NewBodyOperationType.REMOVE, "oppositeDirection" : true, "depth" : 2.54 * mm});
        }
        {
            var Q0;
            Q0=makeQuery(id+"F23.opExtrude","CAP_FACE",FACE,{"disambiguationData":[OSD([sQuery(id+"F22.wireOp",EDGE,"E60"),sQuery(id+"F22.wireOp",EDGE,"E61"),sQuery(id+"F22.wireOp",EDGE,"E63.bottom"),sQuery(id+"F22.wireOp",EDGE,"E63.top"),sQuery(id+"F22.wireOp",EDGE,"E64"),sQuery(id+"F22.wireOp",EDGE,"E65")])],"isStart":false});
            var sketch = newSketch(context, id + "F36", { "sketchPlane" : qUnion([Q0])});
            skArc(sketch, "E89", {"start": v(-6.78, 14.63) * mm, "mid": v(-9.78, 17.63) * mm, "end": v(-12.78, 14.63) * mm});
            skArc(sketch, "E90", {"start": v(-12.78, -5.69) * mm, "mid": v(-9.78, -8.69) * mm, "end": v(-6.78, -5.69) * mm});
            skLineSegment(sketch, "E91", {"start": v(-12.78, -5.69) * mm, "end": v(-12.78, 14.63) * mm});
            skLineSegment(sketch, "E92", {"start": v(-6.78, -5.69) * mm, "end": v(-6.78, 14.63) * mm});
            skCircle(sketch, "E93", {"center": v(-9.78, 14.63) * mm, "radius": 1.52 * mm});
            skCircle(sketch, "E94", {"center": v(-9.78, -5.69) * mm, "radius": 1.52 * mm});
            skSolve(sketch);
        }
        {
            var Q0;
            Q0=qSketchRegion(id+"F36",true);
            extrude(context, id + "F37", {"entities" : qUnion([Q0]), "depth" : 2 * mm});
        }
    });
